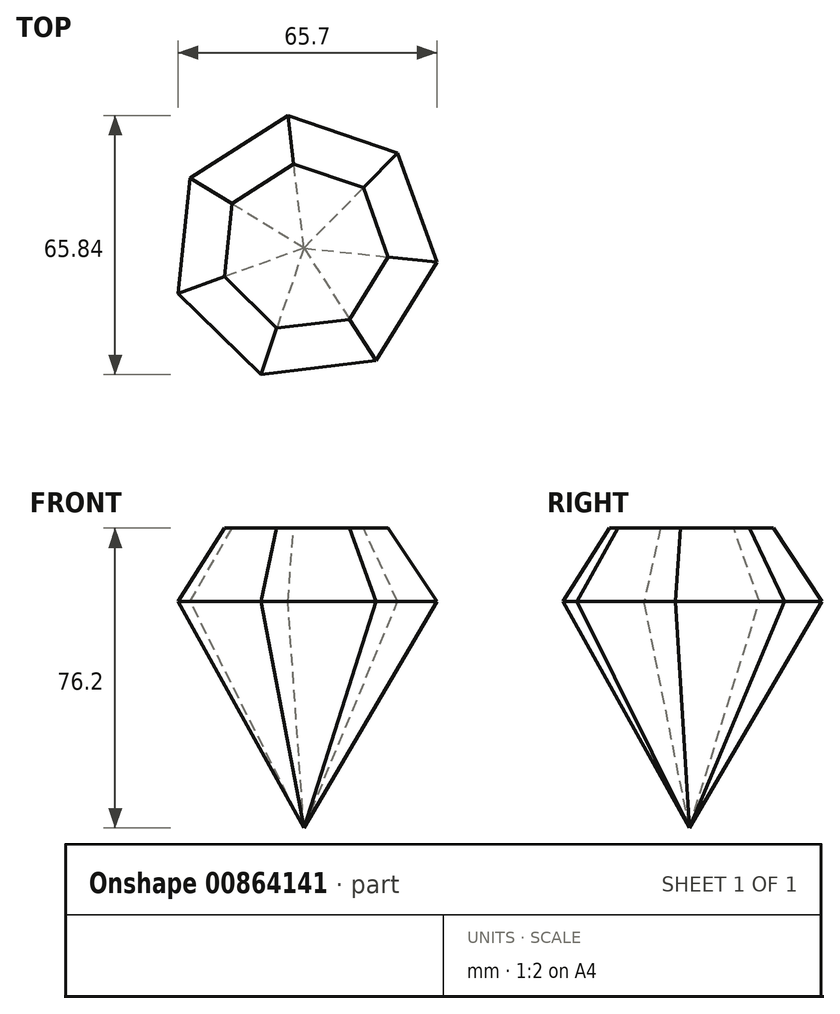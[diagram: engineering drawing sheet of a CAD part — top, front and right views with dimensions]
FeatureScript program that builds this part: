
annotation { "Feature Type Name" : "Feature", "Feature Type Description" : "" }
export const myFeature = defineFeature(function(context is Context, id is Id, definition is map)
    precondition{}
    {
        {
            var Q0;
            Q0=qCreatedBy(makeId("Top.planeOp"),FACE);
            cPlane(context, id + "F0", {"entities" : qUnion([Q0]), "cplaneType" : CPlaneType.OFFSET, "offset" : 76.2 * mm, "width" : 152.4 * mm, "height" : 152.4 * mm});
        }
        {
            var Q0;
            Q0=qCreatedBy(id+"F0.planeOp",FACE);
            var sketch = newSketch(context, id + "F1", { "sketchPlane" : qUnion([Q0])});
            skPoint(sketch, "E0", {"position": v(0, 0) * mm});
            skSolve(sketch);
        }
        {
            var Q0;
            Q0=qCreatedBy(id+"F0.planeOp",FACE);
            cPlane(context, id + "F2", {"entities" : qUnion([Q0]), "cplaneType" : CPlaneType.OFFSET, "offset" : 76.2 * mm, "width" : 152.4 * mm, "height" : 152.4 * mm});
        }
        {
            var Q0;
            Q0=qCreatedBy(id+"F2.planeOp",FACE);
            var sketch = newSketch(context, id + "F3", { "sketchPlane" : qUnion([Q0])});
            skCircle(sketch, "E1.cCircle", {"center": v(0, 0) * mm, "radius": 40.5 * mm, "construction": true});
            skLineSegment(sketch, "E1.0", {"start": v(44.71, -4.64) * mm, "end": v(24.25, -37.85) * mm});
            skLineSegment(sketch, "E1.1", {"start": v(24.25, -37.85) * mm, "end": v(-14.48, -42.56) * mm});
            skLineSegment(sketch, "E1.2", {"start": v(-14.48, -42.56) * mm, "end": v(-42.3, -15.22) * mm});
            skLineSegment(sketch, "E1.3", {"start": v(-42.3, -15.22) * mm, "end": v(-38.27, 23.58) * mm});
            skLineSegment(sketch, "E1.4", {"start": v(-38.27, 23.58) * mm, "end": v(-5.42, 44.62) * mm});
            skLineSegment(sketch, "E1.5", {"start": v(-5.42, 44.62) * mm, "end": v(31.5, 32.06) * mm});
            skLineSegment(sketch, "E1.6", {"start": v(31.5, 32.06) * mm, "end": v(44.71, -4.64) * mm});
            skPoint(sketch, "E1.0.midPoint", {"position": v(34.48, -21.25) * mm});
            skSolve(sketch);
        }
        {
            var Q0;
            Q0=sQuery(id+"F1.wireOp",VERTEX,"E0");
            var Q1;
            Q1=makeQuery(id+"F3.imprint","IMPRINT",FACE,{"disambiguationData":[TD([[makeQuery(id+"F3.imprint","IMPRINT",EDGE,{"derivedFrom":sQuery(id+"F3.wireOp",EDGE,"E1.0")}),-1.0]])]});
            loft(context, id + "F4", {"sheetProfilesArray" : [{ "sheetProfileEntities" : qUnion([Q0]) }, { "sheetProfileEntities" : qUnion([Q1]) }]});
        }
        {
            var Q0;
            Q0=makeQuery(id+"F4.opLoft","CAP_FACE",FACE,{"disambiguationData":[OSD([makeQuery(id+"F3.imprint","IMPRINT",FACE,{"disambiguationData":[TD([[makeQuery(id+"F3.imprint","IMPRINT",EDGE,{"derivedFrom":sQuery(id+"F3.wireOp",EDGE,"E1.0")}),-1.0]])]})])],"isStart":true});
            chamfer(context, id + "F5", {"entities" : qUnion([Q0]), "width" : 12.7 * mm, "tangentPropagation" : true});
        }
    });
